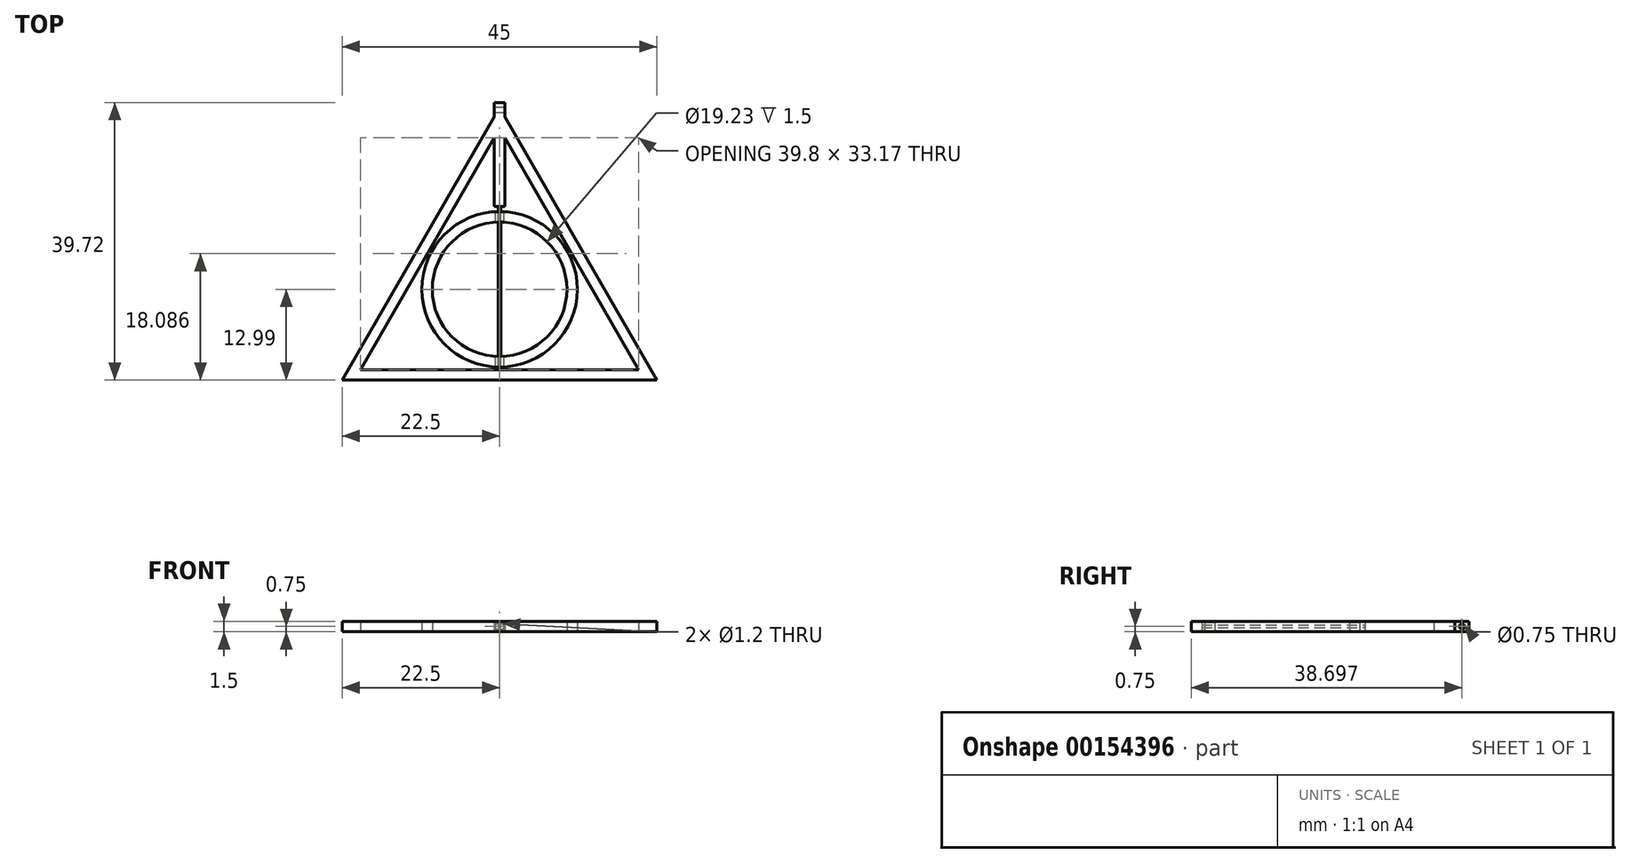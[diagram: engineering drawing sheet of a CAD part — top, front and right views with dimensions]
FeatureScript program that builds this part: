
annotation { "Feature Type Name" : "Feature", "Feature Type Description" : "" }
export const myFeature = defineFeature(function(context is Context, id is Id, definition is map)
    precondition{}
    {
        {
            assignVariable(context, id + "F0", {"name" : "beamThickness", "anyValue" : 1.5});
        }
        {
            var Q0;
            Q0=qCreatedBy(makeId("Top.planeOp"),FACE);
            var sketch = newSketch(context, id + "F1", { "sketchPlane" : qUnion([Q0])});
            skLineSegment(sketch, "E0", {"start": v(0, 34.47) * mm, "end": v(-19.9, 0) * mm});
            skLineSegment(sketch, "E1", {"start": v(-19.9, 0) * mm, "end": v(19.9, 0) * mm});
            skLineSegment(sketch, "E2", {"start": v(19.9, 0) * mm, "end": v(0, 34.47) * mm});
            skCircle(sketch, "E3", {"center": v(0, 11.5) * mm, "radius": 9.62 * mm});
            skLineSegment(sketch, "E4", {"start": v(0, 34.47) * mm, "end": v(0, 11.5) * mm, "construction": true});
            skLineSegment(sketch, "E5", {"start": v(0, 11.5) * mm, "end": v(19.9, 0) * mm, "construction": true});
            skLineSegment(sketch, "E6", {"start": v(-19.9, 0) * mm, "end": v(0, 11.5) * mm, "construction": true});
            skCircle(sketch, "E7.0", {"center": v(0, 11.5) * mm, "radius": 11.12 * mm});
            skLineSegment(sketch, "E8.0", {"start": v(0, 37.47) * mm, "end": v(-22.5, -1.5) * mm});
            skLineSegment(sketch, "E8.1", {"start": v(22.5, -1.5) * mm, "end": v(0, 37.47) * mm});
            skLineSegment(sketch, "E8.2", {"start": v(-22.5, -1.5) * mm, "end": v(22.5, -1.5) * mm});
            skLineSegment(sketch, "E9", {"start": v(-9.95, 17.24) * mm, "end": v(-9.63, 17.05) * mm, "construction": true});
            skLineSegment(sketch, "E10", {"start": v(-0.75, 38.22) * mm, "end": v(0.75, 38.22) * mm});
            skLineSegment(sketch, "E11", {"start": v(0.75, 38.22) * mm, "end": v(0.75, 23.36) * mm});
            skLineSegment(sketch, "E12", {"start": v(0.75, 23.36) * mm, "end": v(-0.75, 23.36) * mm});
            skLineSegment(sketch, "E13", {"start": v(-0.75, 23.36) * mm, "end": v(-0.75, 38.22) * mm});
            skSolve(sketch);
        }
        {
            var Q0;
            Q0 = qSketchRegion(id + "F1", true);
            var Q1;
            {var subQ0=sQuery(id+"F1.wireOp",EDGE,"E12");Q1=makeQuery(id+"F1.imprint","IMPRINT",FACE,{"disambiguationData":[TD([[makeQuery(id+"F1.imprint","IMPRINT",EDGE,{"derivedFrom":subQ0}),-1.0]])]});}
            var Q2;
            Q2=makeQuery(id+"F1.imprint","IMPRINT",FACE,{"disambiguationData":[TD([[makeQuery(id+"F1.imprint","IMPRINT",EDGE,{"derivedFrom":sQuery(id+"F1.wireOp",EDGE,"E3")}),-1.0]])]});
            extrude(context, id + "F2", {"entities" : qUnion([Q0, Q1, Q2]), "depth" : getVariable(context, 'beamThickness') * 1 * mm});
        }
        {
            var Q0;
            Q0=makeQuery(id+"F2.opExtrude","SWEPT_FACE",FACE,{"disambiguationData":[OSD([sQuery(id+"F1.wireOp",EDGE,"E12")])]});
            var sketch = newSketch(context, id + "F3", { "sketchPlane" : qUnion([Q0])});
            skLineSegment(sketch, "E14", {"start": v(-0.75, 0) * mm, "end": v(0.75, 1.5) * mm, "construction": true});
            skCircle(sketch, "E15", {"center": v(0, 0.75) * mm, "radius": 0.2 * mm});
            skCircle(sketch, "E16", {"center": v(0, 0.75) * mm, "radius": 0.6 * mm});
            skSolve(sketch);
        }
        {
            var Q0;
            Q0=makeQuery(id+"F3.imprint","IMPRINT",FACE,{"disambiguationData":[TD([[makeQuery(id+"F3.imprint","IMPRINT",EDGE,{"derivedFrom":sQuery(id+"F3.wireOp",EDGE,"E15")}),-1.0]])]});
            var Q1;
            Q1=makeQuery(id+"F3.imprint","IMPRINT",FACE,{"disambiguationData":[TD([[makeQuery(id+"F3.imprint","IMPRINT",EDGE,{"derivedFrom":sQuery(id+"F3.wireOp",EDGE,"E15")}),1.0]])]});
            var Q2;
            Q2=makeQuery(id+"F2.opExtrude","SWEPT_FACE",FACE,{"disambiguationData":[OSD([sQuery(id+"F1.wireOp",EDGE,"E1")])]});
            extrude(context, id + "F4", {"entities" : qUnion([Q0, Q1]), "operationType" : NewBodyOperationType.REMOVE, "endBound" : BoundingType.UP_TO_SURFACE, "endBoundEntityFace" : qUnion([Q2]), "depth" : 25 * mm});
        }
        {
            var Q0;
            Q0=makeQuery(id+"F3.imprint","IMPRINT",FACE,{"disambiguationData":[TD([[makeQuery(id+"F3.imprint","IMPRINT",EDGE,{"derivedFrom":sQuery(id+"F3.wireOp",EDGE,"E15")}),1.0]])]});
            var Q1;
            Q1=makeQuery(id+"F2.opExtrude","SWEPT_FACE",FACE,{"disambiguationData":[OSD([sQuery(id+"F1.wireOp",EDGE,"E1")])]});
            extrude(context, id + "F5", {"entities" : qUnion([Q0]), "operationType" : NewBodyOperationType.ADD, "endBound" : BoundingType.UP_TO_SURFACE, "endBoundEntityFace" : qUnion([Q1]), "depth" : 25 * mm});
        }
        {
            var Q0;
            {var subQ0=sQuery(id+"F1.wireOp",EDGE,"E11");Q0=makeQuery(id+"F2.opExtrude","SWEPT_FACE",FACE,{"disambiguationData":[OSD([subQ0]),TDD([makeQuery(id+"F1.imprint","IMPRINT",EDGE,{"disambiguationData":[TD([[makeQuery(id+"F1.imprint","INTERSECT",VERTEX,{"derivedFrom":[sQuery(id+"F1.wireOp",EDGE,"E10"),subQ0]}),-1.0]])],"derivedFrom":subQ0})])]});}
            var sketch = newSketch(context, id + "F6", { "sketchPlane" : qUnion([Q0])});
            skCircle(sketch, "E17", {"center": v(37.2, 0.75) * mm, "radius": 0.38 * mm});
            skPoint(sketch, "E17.centerSnap0", {"position": v(37.2, 1.5) * mm});
            skPoint(sketch, "E17.centerSnap1", {"position": v(36.17, 0.75) * mm});
            skSolve(sketch);
        }
        {
            var Q0;
            Q0 = qSketchRegion(id + "F6", true);
            var Q1;
            {var subQ0=sQuery(id+"F1.wireOp",EDGE,"E13");Q1=makeQuery(id+"F2.opExtrude","SWEPT_FACE",FACE,{"disambiguationData":[OSD([subQ0]),TDD([makeQuery(id+"F1.imprint","IMPRINT",EDGE,{"disambiguationData":[TD([[makeQuery(id+"F1.imprint","INTERSECT",VERTEX,{"derivedFrom":[sQuery(id+"F1.wireOp",EDGE,"E10"),subQ0]}),1.0]])],"derivedFrom":subQ0})])]});}
            extrude(context, id + "F7", {"entities" : qUnion([Q0]), "operationType" : NewBodyOperationType.REMOVE, "endBound" : BoundingType.UP_TO_SURFACE, "oppositeDirection" : true, "endBoundEntityFace" : qUnion([Q1]), "depth" : 25 * mm});
        }
    });
